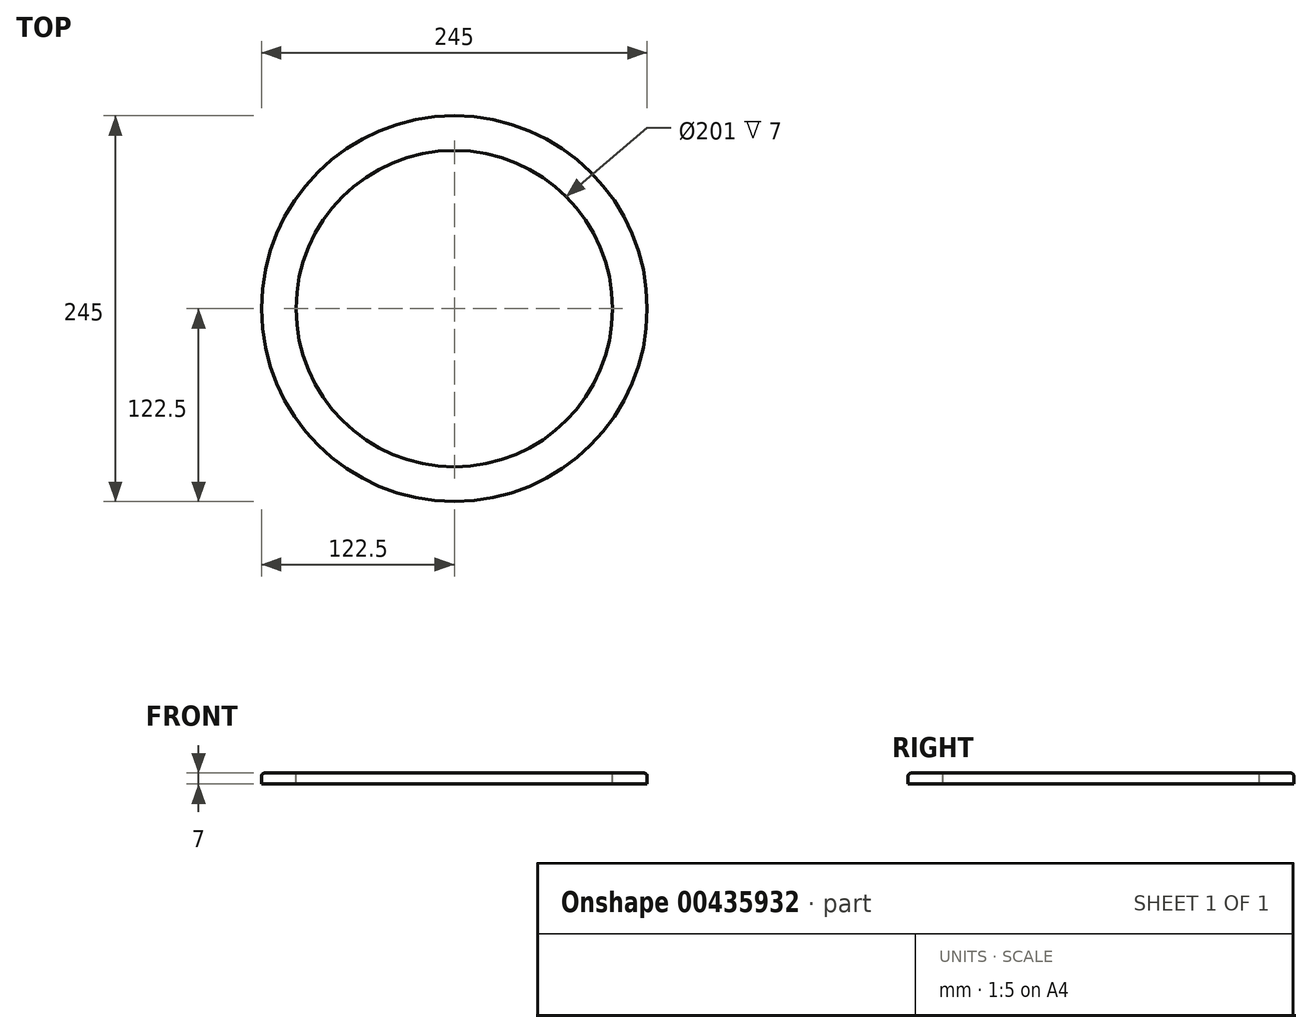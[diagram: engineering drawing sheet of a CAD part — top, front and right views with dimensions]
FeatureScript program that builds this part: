
annotation { "Feature Type Name" : "Feature", "Feature Type Description" : "" }
export const myFeature = defineFeature(function(context is Context, id is Id, definition is map)
    precondition{}
    {
        {
            var Q0;
            Q0=qCreatedBy(makeId("Top.planeOp"),FACE);
            var sketch = newSketch(context, id + "F0", { "sketchPlane" : qUnion([Q0])});
            skCircle(sketch, "E0", {"center": v(0, 0) * mm, "radius": 122.5 * mm});
            skSolve(sketch);
        }
        {
            var Q0;
            Q0=makeQuery(id+"F0.imprint","IMPRINT",FACE,{"disambiguationData":[TD([[makeQuery(id+"F0.imprint","IMPRINT",EDGE,{"derivedFrom":sQuery(id+"F0.wireOp",EDGE,"E0")}),1.0]])]});
            extrude(context, id + "F1", {"entities" : qUnion([Q0]), "depth" : 7 * mm});
        }
        {
            var Q0;
            Q0=makeQuery(id+"F1.opExtrude","CAP_FACE",FACE,{"disambiguationData":[OSD([sQuery(id+"F0.wireOp",EDGE,"E0")])],"isStart":false});
            var sketch = newSketch(context, id + "F2", { "sketchPlane" : qUnion([Q0])});
            skCircle(sketch, "E1", {"center": v(0, 0) * mm, "radius": 100.5 * mm});
            skSolve(sketch);
        }
        {
            var Q0;
            Q0 = qSketchRegion(id + "F2", true);
            extrude(context, id + "F3", {"entities" : qUnion([Q0]), "operationType" : NewBodyOperationType.REMOVE, "oppositeDirection" : true, "depth" : 25 * mm});
        }
        {
            var Q0;
            Q0=makeQuery(id+"F1.opExtrude","CAP_EDGE",EDGE,{"disambiguationData":[OSD([sQuery(id+"F0.wireOp",EDGE,"E0")])],"isStart":false});
            var Q1;
            Q1=makeQuery(id+"F3.boolean.opBoolean","COPY",EDGE,{"derivedFrom":makeQuery(id+"F3.opExtrude","CAP_EDGE",EDGE,{"disambiguationData":[OSD([sQuery(id+"F2.wireOp",EDGE,"E1")])],"isStart":true})});
            fillet(context, id + "F4", {"entities" : qUnion([Q0, Q1]), "radius" : 2 * mm, "tangentPropagation" : true, "allowEdgeOverflow" : false});
        }
    });
